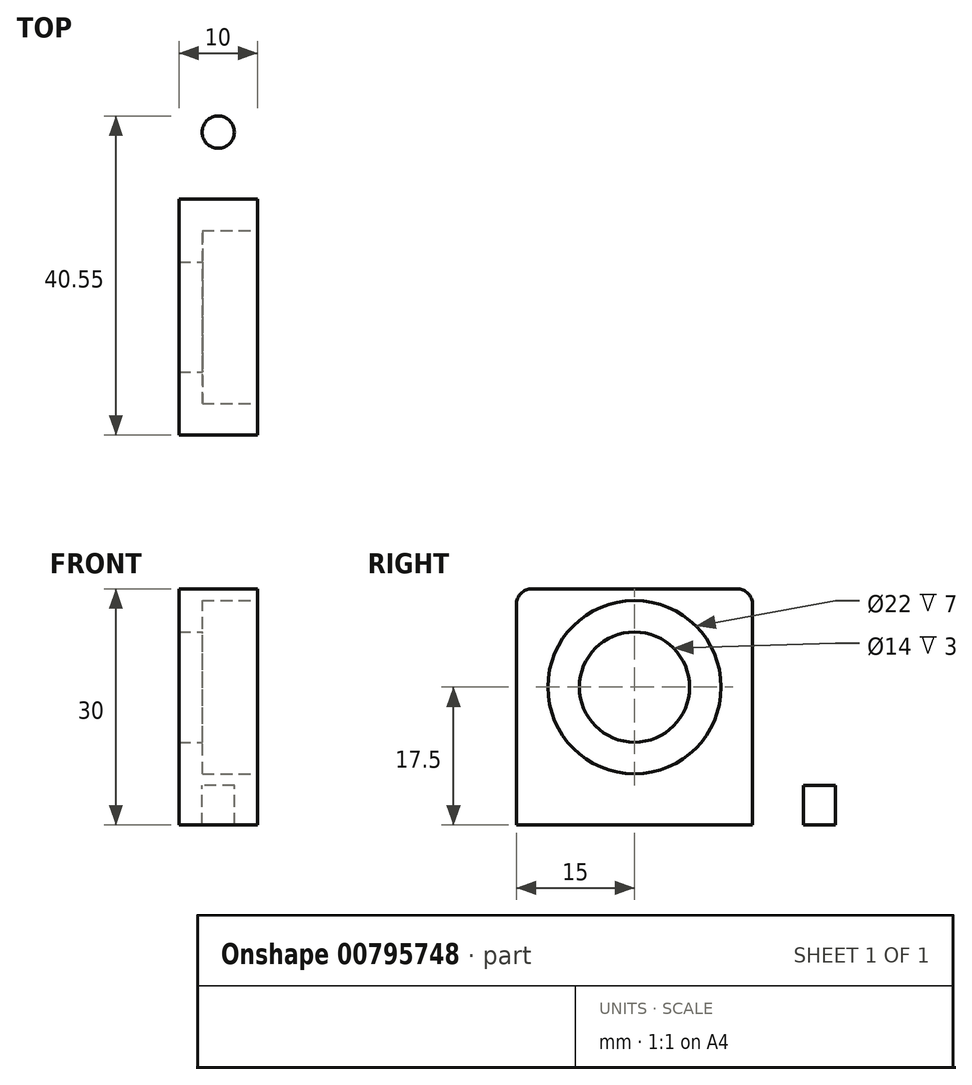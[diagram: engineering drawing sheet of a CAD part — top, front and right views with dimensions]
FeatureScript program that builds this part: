
annotation { "Feature Type Name" : "Feature", "Feature Type Description" : "" }
export const myFeature = defineFeature(function(context is Context, id is Id, definition is map)
    precondition{}
    {
        {
            var Q0;
            Q0=qCreatedBy(makeId("Top.planeOp"),FACE);
            var sketch = newSketch(context, id + "F0", { "sketchPlane" : qUnion([Q0])});
            skLineSegment(sketch, "E0.bottom", {"start": v(7.5, -27.5) * mm, "end": v(-7.5, -27.5) * mm});
            skLineSegment(sketch, "E0.top", {"start": v(7.5, 27.5) * mm, "end": v(-7.5, 27.5) * mm});
            skLineSegment(sketch, "E0.left", {"start": v(7.5, -27.5) * mm, "end": v(7.5, 27.5) * mm});
            skLineSegment(sketch, "E0.right", {"start": v(-7.5, -27.5) * mm, "end": v(-7.5, 27.5) * mm});
            skPoint(sketch, "E0.middle", {"position": v(0, 0) * mm});
            skSolve(sketch);
        }
        {
            var Q0;
            Q0 = qSketchRegion(id + "F0", true);
            extrude(context, id + "F1", {"entities" : qUnion([Q0]), "depth" : 5 * mm, "offsetDistance" : 25 * mm});
        }
        {
            var Q0;
            Q0=makeQuery(id+"F1.opExtrude","CAP_FACE",FACE,{"disambiguationData":[OSD([sQuery(id+"F0.wireOp",EDGE,"E0.bottom"),sQuery(id+"F0.wireOp",EDGE,"E0.top"),sQuery(id+"F0.wireOp",EDGE,"E0.left"),sQuery(id+"F0.wireOp",EDGE,"E0.right")])],"isStart":false});
            var sketch = newSketch(context, id + "F2", { "sketchPlane" : qUnion([Q0])});
            skLineSegment(sketch, "E1.bottom", {"start": v(5, -15) * mm, "end": v(-5, -15) * mm});
            skLineSegment(sketch, "E1.top", {"start": v(5, 15) * mm, "end": v(-5, 15) * mm});
            skLineSegment(sketch, "E1.left", {"start": v(5, -15) * mm, "end": v(5, 15) * mm});
            skLineSegment(sketch, "E1.right", {"start": v(-5, -15) * mm, "end": v(-5, 15) * mm});
            skPoint(sketch, "E1.middle", {"position": v(0, 0) * mm});
            skSolve(sketch);
        }
        {
            var Q0;
            Q0=makeQuery(id+"F2.imprint","IMPRINT",FACE,{"disambiguationData":[TD([[makeQuery(id+"F2.imprint","IMPRINT",EDGE,{"derivedFrom":sQuery(id+"F2.wireOp",EDGE,"E1.bottom")}),-1.0]])]});
            extrude(context, id + "F3", {"entities" : qUnion([Q0]), "operationType" : NewBodyOperationType.ADD, "depth" : 25 * mm, "offsetDistance" : 25 * mm});
        }
        {
            var Q0;
            Q0=makeQuery(id+"F3.opExtrude","SWEPT_FACE",FACE,{"disambiguationData":[OSD([sQuery(id+"F2.wireOp",EDGE,"E1.left")])]});
            var sketch = newSketch(context, id + "F4", { "sketchPlane" : qUnion([Q0])});
            skLineSegment(sketch, "E2", {"start": v(0, 30) * mm, "end": v(0, 17.5) * mm, "construction": true});
            skCircle(sketch, "E3", {"center": v(0, 17.5) * mm, "radius": 11 * mm});
            skSolve(sketch);
        }
        {
            var Q0;
            Q0=makeQuery(id+"F4.imprint","IMPRINT",FACE,{"disambiguationData":[TD([[makeQuery(id+"F4.imprint","IMPRINT",EDGE,{"derivedFrom":sQuery(id+"F4.wireOp",EDGE,"E3")}),1.0]])]});
            extrude(context, id + "F5", {"entities" : qUnion([Q0]), "operationType" : NewBodyOperationType.REMOVE, "oppositeDirection" : true, "depth" : 7 * mm, "offsetDistance" : 25 * mm});
        }
        {
            var Q0;
            Q0=makeQuery(id+"F1.opExtrude","CAP_FACE",FACE,{"disambiguationData":[OSD([sQuery(id+"F0.wireOp",EDGE,"E0.bottom"),sQuery(id+"F0.wireOp",EDGE,"E0.top"),sQuery(id+"F0.wireOp",EDGE,"E0.left"),sQuery(id+"F0.wireOp",EDGE,"E0.right")])],"isStart":false});
            var sketch = newSketch(context, id + "F6", { "sketchPlane" : qUnion([Q0])});
            skCircle(sketch, "E4", {"center": v(0, -23.5) * mm, "radius": 2 * mm});
            skPoint(sketch, "E4.centerSnap0", {"position": v(0, -27.5) * mm});
            skCircle(sketch, "E5.MirrorC", {"center": v(0, 23.5) * mm, "radius": 2.05 * mm});
            skSolve(sketch);
        }
        {
            var Q0;
            Q0=makeQuery(id+"F6.imprint","IMPRINT",FACE,{"disambiguationData":[TD([[makeQuery(id+"F6.imprint","IMPRINT",EDGE,{"derivedFrom":sQuery(id+"F6.wireOp",EDGE,"E4")}),1.0]])]});
            var Q1;
            Q1=makeQuery(id+"F6.imprint","IMPRINT",FACE,{"disambiguationData":[TD([[makeQuery(id+"F6.imprint","IMPRINT",EDGE,{"derivedFrom":sQuery(id+"F6.wireOp",EDGE,"E5.MirrorC")}),-1.0]])]});
            extrude(context, id + "F7", {"entities" : qUnion([Q0, Q1]), "operationType" : NewBodyOperationType.REMOVE, "oppositeDirection" : true, "depth" : 25 * mm, "offsetDistance" : 25 * mm});
        }
        {
            var Q0;
            Q0=makeQuery(id+"F3.opExtrude","CAP_EDGE",EDGE,{"disambiguationData":[OSD([sQuery(id+"F2.wireOp",EDGE,"E1.bottom")])],"isStart":false});
            var Q1;
            Q1=makeQuery(id+"F3.opExtrude","CAP_EDGE",EDGE,{"disambiguationData":[OSD([sQuery(id+"F2.wireOp",EDGE,"E1.bottom")])],"isStart":true});
            var Q2;
            Q2=makeQuery(id+"F3.opExtrude","CAP_EDGE",EDGE,{"disambiguationData":[OSD([sQuery(id+"F2.wireOp",EDGE,"E1.left")])],"isStart":true});
            var Q3;
            Q3=makeQuery(id+"F3.opExtrude","CAP_EDGE",EDGE,{"disambiguationData":[OSD([sQuery(id+"F2.wireOp",EDGE,"E1.top")])],"isStart":false});
            var Q4;
            Q4=makeQuery(id+"F3.opExtrude","CAP_EDGE",EDGE,{"disambiguationData":[OSD([sQuery(id+"F2.wireOp",EDGE,"E1.top")])],"isStart":true});
            var Q5;
            Q5=makeQuery(id+"F3.opExtrude","CAP_EDGE",EDGE,{"disambiguationData":[OSD([sQuery(id+"F2.wireOp",EDGE,"E1.right")])],"isStart":true});
            fillet(context, id + "F8", {"entities" : qUnion([Q0, Q1, Q2, Q3, Q4, Q5]), "radius" : 2 * mm, "tangentPropagation" : true, "allowEdgeOverflow" : false});
        }
        {
            var Q0;
            Q0=makeQuery(id+"F5.boolean.opBoolean","COPY",FACE,{"derivedFrom":makeQuery(id+"F5.opExtrude","CAP_FACE",FACE,{"disambiguationData":[OSD([sQuery(id+"F4.wireOp",EDGE,"E3")])],"isStart":false})});
            var sketch = newSketch(context, id + "F9", { "sketchPlane" : qUnion([Q0])});
            skCircle(sketch, "E6", {"center": v(0, 17.5) * mm, "radius": 7 * mm});
            skSolve(sketch);
        }
        {
            var Q0;
            Q0=makeQuery(id+"F9.imprint","IMPRINT",FACE,{"disambiguationData":[TD([[makeQuery(id+"F9.imprint","IMPRINT",EDGE,{"derivedFrom":sQuery(id+"F9.wireOp",EDGE,"E6")}),1.0]])]});
            extrude(context, id + "F10", {"entities" : qUnion([Q0]), "operationType" : NewBodyOperationType.REMOVE, "endBound" : BoundingType.THROUGH_ALL, "oppositeDirection" : true, "depth" : 25 * mm, "offsetDistance" : 25 * mm});
        }
    });
